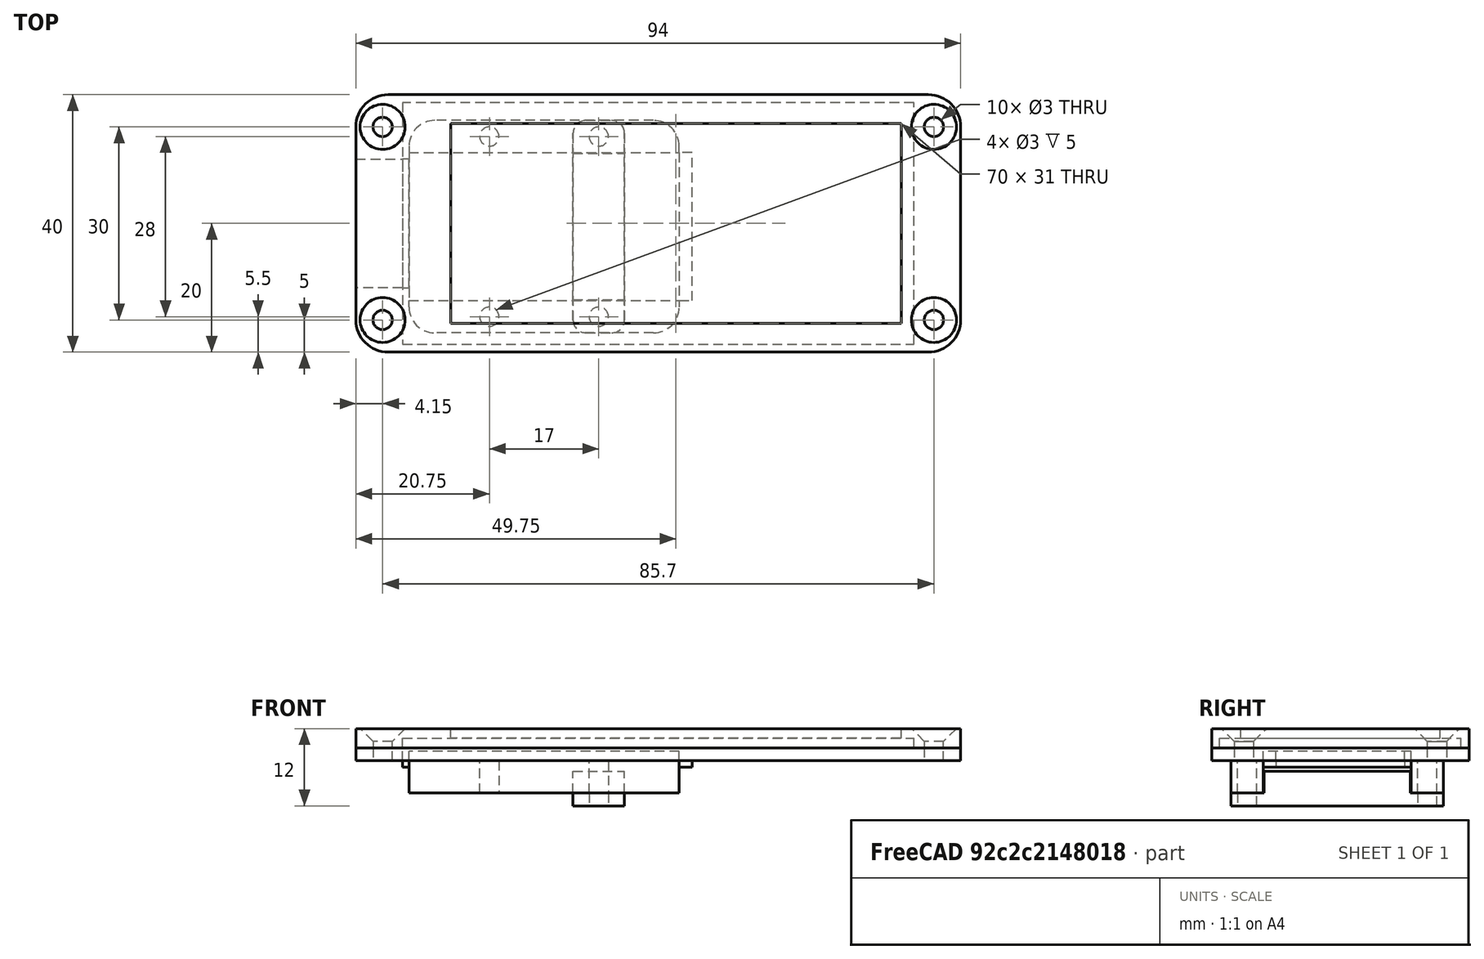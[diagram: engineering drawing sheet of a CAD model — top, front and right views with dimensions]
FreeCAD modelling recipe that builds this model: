
FCSTD DOCUMENT  (FreeCAD 0.19R)
Label: CrocSaintGerard
License: All rights reserved
LicenseURL: http://en.wikipedia.org/wiki/All_rights_reserved
objects: Sketcher::SketchObject×23, PartDesign::Pad×11, PartDesign::Body×8, PartDesign::Pocket×6, PartDesign::Fillet×6, PartDesign::Revolution×2, PartDesign::Chamfer×1, App::VRMLObject×1, Part::Helix×1, PartDesign::ShapeBinder×1, PartDesign::AdditivePipe×1, PartDesign::LinearPattern×1, App::DocumentObjectGroup×1, Mesh::Feature×1
note: 88 computed .brp shape members not serialized (recipe doc carries the construction recipe); baked Part::Feature solids carry a one-line shape summary decoded from their .brp

FEATURE [Sketcher::SketchObject] Sketch
  FullyConstrained = false
  MapMode = 5
  Support = -> [XY_Plane]
  sketch-geometry (17):
    g0: LineSegment StartX=-47 StartY=20 StartZ=0 EndX=47 EndY=20 EndZ=0
    g1: LineSegment StartX=47 StartY=20 StartZ=0 EndX=47 EndY=-20 EndZ=0
    g2: LineSegment StartX=47 StartY=-20 StartZ=0 EndX=-47 EndY=-20 EndZ=0
    g3: LineSegment StartX=-39.75 StartY=18.75 StartZ=0 EndX=39.75 EndY=18.75 EndZ=0
    g4: LineSegment StartX=39.75 StartY=18.75 StartZ=0 EndX=39.75 EndY=-18.75 EndZ=0
    g5: LineSegment StartX=39.75 StartY=-18.75 StartZ=0 EndX=-39.75 EndY=-18.75 EndZ=0
    g6: LineSegment StartX=-39.75 StartY=-18.75 StartZ=0 EndX=-39.75 EndY=18.75 EndZ=0
    g7: Circle CenterX=-42.85 CenterY=15 CenterZ=0 NormalX=0 NormalY=0 NormalZ=1 AngleXU=0 Radius=1.5
    g8: Circle CenterX=-42.85 CenterY=-15 CenterZ=0 NormalX=0 NormalY=0 NormalZ=1 AngleXU=0 Radius=1.5
    g9: Circle CenterX=42.85 CenterY=-15 CenterZ=0 NormalX=0 NormalY=0 NormalZ=1 AngleXU=0 Radius=1.5
    g10: Circle CenterX=42.85 CenterY=15 CenterZ=0 NormalX=0 NormalY=0 NormalZ=1 AngleXU=0 Radius=1.5
    g11: Circle CenterX=-42.85 CenterY=15 CenterZ=0 NormalX=0 NormalY=0 NormalZ=1 AngleXU=0 Radius=3
    g12: LineSegment StartX=-47 StartY=20 StartZ=0 EndX=-47 EndY=10 EndZ=0
    g13: LineSegment StartX=-47 StartY=10 StartZ=0 EndX=-39.75 EndY=10 EndZ=0
    g14: LineSegment StartX=-39.75 StartY=10 StartZ=0 EndX=-39.75 EndY=-10 EndZ=0
    g15: LineSegment StartX=-39.75 StartY=-10 StartZ=0 EndX=-47 EndY=-10 EndZ=0
    g16: LineSegment StartX=-47 StartY=-10 StartZ=0 EndX=-47 EndY=-20 EndZ=0
  constraints (44):
    c: Coincident(g0,g1)
    c: Coincident(g1,g2)
    c: Horizontal(g0)
    c: Horizontal(g2)
    c: Vertical(g1)
    c: Symmetric(g0,g1,g-1)
    c: DistanceY(g1,g1) = 40
    c: DistanceX(g0,g0) = 94
    c: Coincident(g3,g4)
    c: Coincident(g4,g5)
    c: Coincident(g5,g6)
    c: Coincident(g6,g3)
    c: Horizontal(g3)
    c: Horizontal(g5)
    c: Vertical(g4)
    c: Vertical(g6)
    c: Symmetric(g3,g4,g-1)
    c: DistanceY(g6,g6) = 37.5
    c: DistanceX(g3,g3) = 79.5
    c: Radius(g10) = 1.5
    c: Equal(g10,g9)
    c: Equal(g10,g8)
    c: Equal(g10,g7)
    c: Symmetric(g7,g8,g-1)
    c: Symmetric(g10,g9,g-1)
    c: Symmetric(g10,g7,g-2)
    c: Coincident(g11,g7)
    c: Radius(g11) = 3
    c: Coincident(g0,g12)
    c: Vertical(g12)
    c: Coincident(g12,g13)
    c: Horizontal(g13)
    c: Coincident(g13,g14)
    c: Vertical(g14)
    c: Coincident(g14,g15)
    c: Horizontal(g15)
    c: Coincident(g15,g16)
    c: Coincident(g16,g2)
    c: Vertical(g16)
    c: Symmetric(g15,g12,g-1)
    c: PointOnObject(g13,g6)
    c: DistanceY(g14,g14) = 20
    c: DistanceY(g-1,g7) = 15
    c: DistanceX(g-2,g7) = -42.85
FEATURE [PartDesign::Pad] Pad
  AllowMultiFace = false
  Direction = (1,1,1)
  Length = 2
  Length2 = 100
  Profile = -> Sketch
  Type = 0
FEATURE [Sketcher::SketchObject] Sketch001
  FullyConstrained = true
  MapMode = 5
  Support = -> [XY_Plane001]
  sketch-geometry (16):
    g0: LineSegment StartX=-47 StartY=20 StartZ=0 EndX=47 EndY=20 EndZ=0
    g1: LineSegment StartX=47 StartY=20 StartZ=0 EndX=47 EndY=-20 EndZ=0
    g2: LineSegment StartX=47 StartY=-20 StartZ=0 EndX=-47 EndY=-20 EndZ=0
    g3: LineSegment StartX=-47 StartY=-20 StartZ=0 EndX=-47 EndY=20 EndZ=0
    g4: Circle CenterX=-42.85 CenterY=15 CenterZ=0 NormalX=0 NormalY=0 NormalZ=1 AngleXU=0 Radius=1.5
    g5: Circle CenterX=-42.85 CenterY=-15 CenterZ=0 NormalX=0 NormalY=0 NormalZ=1 AngleXU=0 Radius=1.5
    g6: Circle CenterX=42.85 CenterY=15 CenterZ=0 NormalX=0 NormalY=0 NormalZ=1 AngleXU=0 Radius=1.5
    g7: Circle CenterX=42.85 CenterY=-15 CenterZ=0 NormalX=0 NormalY=0 NormalZ=1 AngleXU=0 Radius=1.5
    g8: LineSegment StartX=-32.25 StartY=15.5 StartZ=0 EndX=37.75 EndY=15.5 EndZ=0
    g9: LineSegment StartX=37.75 StartY=15.5 StartZ=0 EndX=37.75 EndY=-15.5 EndZ=0
    g10: LineSegment StartX=37.75 StartY=-15.5 StartZ=0 EndX=-32.25 EndY=-15.5 EndZ=0
    g11: LineSegment StartX=-32.25 StartY=-15.5 StartZ=0 EndX=-32.25 EndY=15.5 EndZ=0
    g12: LineSegment StartX=-39.75 StartY=18.75 StartZ=0 EndX=39.75 EndY=18.75 EndZ=0
    g13: LineSegment StartX=39.75 StartY=18.75 StartZ=0 EndX=39.75 EndY=-18.75 EndZ=0
    g14: LineSegment StartX=39.75 StartY=-18.75 StartZ=0 EndX=-39.75 EndY=-18.75 EndZ=0
    g15: LineSegment StartX=-39.75 StartY=-18.75 StartZ=0 EndX=-39.75 EndY=18.75 EndZ=0
  constraints (42):
    c: Coincident(g0,g1)
    c: Coincident(g1,g2)
    c: Coincident(g2,g3)
    c: Coincident(g3,g0)
    c: Horizontal(g0)
    c: Horizontal(g2)
    c: Vertical(g1)
    c: Vertical(g3)
    c: Symmetric(g1,g0,g-1)
    c: DistanceX(g0,g0) = 94
    c: DistanceY(g3,g3) = 40
    c: Radius(g4) = 1.5
    c: Equal(g4,g6)
    c: Equal(g4,g5)
    c: Equal(g4,g7)
    c: Symmetric(g5,g4,g-1)
    c: Symmetric(g6,g7,g-1)
    c: Symmetric(g4,g6,g-2)
    c: DistanceY(g-1,g4) = 15
    c: DistanceX(g-2,g4) = -42.85
    c: Coincident(g8,g9)
    c: Coincident(g9,g10)
    c: Coincident(g10,g11)
    c: Coincident(g11,g8)
    c: Horizontal(g8)
    c: Horizontal(g10)
    c: Vertical(g11)
    c: DistanceY(g9,g9) = 31
    c: DistanceX(g8,g8) = 70
    c: Symmetric(g8,g9,g-1)
    c: Coincident(g12,g13)
    c: Coincident(g13,g14)
    c: Coincident(g14,g15)
    c: Coincident(g15,g12)
    c: Horizontal(g12)
    c: Horizontal(g14)
    c: Vertical(g13)
    c: Vertical(g15)
    c: DistanceX(g12,g12) = 79.5
    c: Symmetric(g12,g13,g-1)
    c: DistanceY(g15,g15) = 37.5
    c: Distance(g8,g13) = 2
FEATURE [PartDesign::Pad] Pad001
  AllowMultiFace = false
  Direction = (1,1,1)
  Length = 3
  Length2 = 100
  Profile = -> Sketch001
  Type = 0
FEATURE [Sketcher::SketchObject] Sketch002
  FullyConstrained = true
  MapMode = 5
  Placement = pos=(0,0,0) rot=(1,0,0;3.14159rad)
  Support = -> [Pad001]
  sketch-geometry (4):
    g0: LineSegment StartX=-39.75 StartY=18.75 StartZ=0 EndX=39.75 EndY=18.75 EndZ=0
    g1: LineSegment StartX=39.75 StartY=18.75 StartZ=0 EndX=39.75 EndY=-18.75 EndZ=0
    g2: LineSegment StartX=39.75 StartY=-18.75 StartZ=0 EndX=-39.75 EndY=-18.75 EndZ=0
    g3: LineSegment StartX=-39.75 StartY=-18.75 StartZ=0 EndX=-39.75 EndY=18.75 EndZ=0
  constraints (11):
    c: Coincident(g0,g1)
    c: Coincident(g1,g2)
    c: Coincident(g2,g3)
    c: Coincident(g3,g0)
    c: Horizontal(g0)
    c: Horizontal(g2)
    c: Vertical(g1)
    c: Vertical(g3)
    c: DistanceY(g1,g1) = 37.5
    c: DistanceX(g0,g0) = 79.5
    c: Symmetric(g0,g2,g-1)
FEATURE [PartDesign::Pocket] Pocket
  AllowMultiFace = false
  BaseFeature = -> Pad001
  Length = 1.5
  Length2 = 100
  Profile = -> Sketch002
  Type = 0
FEATURE [PartDesign::Fillet] Fillet
  Base = -> Pocket [Edge5,Edge1,Edge8,Edge2]
  BaseFeature = -> Pocket
  Radius = 5
  SupportTransform = false
FEATURE [PartDesign::Fillet] Fillet001
  Base = -> Pad [Edge8,Edge5,Edge11,Edge1]
  BaseFeature = -> Pad
  Radius = 5
  SupportTransform = false
FEATURE [PartDesign::Chamfer] Chamfer
  Angle = 45
  Base = -> Fillet [Edge33,Edge34,Edge35,Edge36]
  BaseFeature = -> Fillet
  ChamferType = 0
  FlipDirection = false
  Size = 2
  Size2 = 1
  SupportTransform = false
FEATURE [PartDesign::Body] Body001  label="Devant"
  Group = -> [Sketch001,Pad001,Sketch002,Pocket,Fillet,Chamfer]
  Origin = -> Origin001
  Placement = pos=(77,-1,19) rot=(0,0,1;0rad)
  Tip = -> Chamfer
FEATURE [Sketcher::SketchObject] Sketch003
  ExternalGeometry = -> [Fillet001]
  FullyConstrained = false
  MapMode = 5
  Placement = pos=(0,0,0) rot=(1,0,0;3.14159rad)
  Support = -> [Fillet001]
  sketch-geometry (4):
    g0: LineSegment StartX=-38.75 StartY=12 StartZ=0 EndX=3.25 EndY=12 EndZ=0
    g1: LineSegment StartX=3.25 StartY=12 StartZ=0 EndX=3.25 EndY=-11 EndZ=0
    g2: LineSegment StartX=3.25 StartY=-11 StartZ=0 EndX=-38.75 EndY=-11 EndZ=0
    g3: LineSegment StartX=-38.75 StartY=-11 StartZ=0 EndX=-38.75 EndY=12 EndZ=0
  constraints (12):
    c: Coincident(g0,g1)
    c: Coincident(g1,g2)
    c: Coincident(g2,g3)
    c: Coincident(g3,g0)
    c: Horizontal(g0)
    c: Horizontal(g2)
    c: Vertical(g1)
    c: Vertical(g3)
    c: DistanceY(g1,g1) = 23
    c: DistanceX(g0,g0) = 42
    c: DistanceY(g-1,g0) = 12
    c: Distance(g0,g-3) = 1
FEATURE [PartDesign::Pocket] Pocket001
  AllowMultiFace = false
  BaseFeature = -> Fillet001
  Length = 1.5
  Length2 = 100
  Profile = -> Sketch003
  Type = 0
FEATURE [Sketcher::SketchObject] Sketch004
  ExternalGeometry = -> [Pocket001]
  FullyConstrained = false
  MapMode = 5
  Placement = pos=(0,0,0) rot=(1,0,0;3.14159rad)
  Support = -> [Pocket001]
  sketch-geometry (18):
    g0: LineSegment StartX=-38.75 StartY=12 StartZ=0 EndX=3.25 EndY=12 EndZ=0
    g1: LineSegment StartX=3.25 StartY=12 StartZ=0 EndX=3.25 EndY=17 EndZ=0
    g2: LineSegment StartX=3.25 StartY=17 StartZ=0 EndX=-38.75 EndY=17 EndZ=0
    g3: LineSegment StartX=-38.75 StartY=17 StartZ=0 EndX=-38.75 EndY=12 EndZ=0
    g4: LineSegment StartX=-38.75 StartY=-11 StartZ=0 EndX=3.25 EndY=-11 EndZ=0
    g5: LineSegment StartX=3.25 StartY=-11 StartZ=0 EndX=3.25 EndY=-16 EndZ=0
    g6: LineSegment StartX=3.25 StartY=-16 StartZ=0 EndX=-38.75 EndY=-16 EndZ=0
    g7: LineSegment StartX=-38.75 StartY=-16 StartZ=0 EndX=-38.75 EndY=-11 EndZ=0
    g8: Circle CenterX=-26.25 CenterY=14.5 CenterZ=0 NormalX=0 NormalY=0 NormalZ=1 AngleXU=0 Radius=1.5
    g9: Circle CenterX=-9.25 CenterY=14.5 CenterZ=0 NormalX=0 NormalY=0 NormalZ=1 AngleXU=0 Radius=1.5
    g10: Circle CenterX=-26.25 CenterY=-13.5 CenterZ=0 NormalX=0 NormalY=0 NormalZ=1 AngleXU=0 Radius=1.5
    g11: Circle CenterX=-9.25 CenterY=-13.5 CenterZ=0 NormalX=0 NormalY=0 NormalZ=1 AngleXU=0 Radius=1.5
    g12: LineSegment StartX=-38.75 StartY=14.5 StartZ=0 EndX=3.25 EndY=14.5 EndZ=0
    g13: LineSegment StartX=-38.75 StartY=14.5 StartZ=0 EndX=-38.75 EndY=17 EndZ=0
    g14: LineSegment StartX=-38.75 StartY=14.5 StartZ=0 EndX=-38.7607 EndY=12 EndZ=0
    g15: LineSegment StartX=-38.75 StartY=-13.5 StartZ=0 EndX=3.25 EndY=-13.5 EndZ=0
    g16: LineSegment StartX=-38.75 StartY=-11 StartZ=0 EndX=-38.75 EndY=-13.1302 EndZ=0
    g17: LineSegment StartX=-38.75 StartY=-16 StartZ=0 EndX=-38.75 EndY=-13.5 EndZ=0
  constraints (47):
    c: Coincident(g0,g1)
    c: Coincident(g1,g2)
    c: Coincident(g2,g3)
    c: Coincident(g3,g0)
    c: Horizontal(g2)
    c: Vertical(g1)
    c: Vertical(g3)
    c: Coincident(g0,g-3)
    c: Coincident(g4,g5)
    c: Coincident(g5,g6)
    c: Coincident(g6,g7)
    c: Coincident(g7,g4)
    c: Horizontal(g6)
    c: Vertical(g5)
    c: Vertical(g7)
    c: Coincident(g4,g-4)
    c: Coincident(g4,g-4)
    c: Coincident(g0,g-3)
    c: Equal(g1,g5)
    c: DistanceY(g1,g1) = 5
    c: Radius(g11) = 1.5
    c: Equal(g11,g10)
    c: Equal(g11,g8)
    c: Equal(g11,g9)
    c: PointOnObject(g12,g3)
    c: PointOnObject(g12,g1)
    c: Horizontal(g12)
    c: Coincident(g13,g12)
    c: Coincident(g13,g2)
    c: PointOnObject(g8,g12)
    c: PointOnObject(g9,g12)
    c: Distance(g14) = 2.5
    c: Coincident(g14,g12)
    c: Distance(g8,g3) = 12.5
    c: Distance(g9,g1) = 12.5
    c: PointOnObject(g15,g7)
    c: PointOnObject(g15,g5)
    c: Horizontal(g15)
    c: Coincident(g16,g4)
    c: PointOnObject(g10,g15)
    c: PointOnObject(g11,g15)
    c: Distance(g10,g7) = 12.5
    c: Distance(g11,g5) = 12.5
    c: Coincident(g17,g6)
    c: Distance(g17) = 2.5
    c: Coincident(g17,g15)
    c: Distance(g13) = 2.5
FEATURE [PartDesign::Pad] Pad002
  AllowMultiFace = false
  BaseFeature = -> Pocket001
  Direction = (1,1,1)
  Length = 5
  Length2 = 100
  Profile = -> Sketch004
  Type = 0
FEATURE [PartDesign::Fillet] Fillet002
  Base = -> Pad002 [Edge58,Edge66,Edge55,Edge68]
  BaseFeature = -> Pad002
  Radius = 4
  SupportTransform = false
FEATURE [Sketcher::SketchObject] Sketch005
  FullyConstrained = false
  MapMode = 5
  Placement = pos=(0,0,0) rot=(0.57735,0.57735,0.57735;2.0944rad)
  Support = -> [YZ_Plane002]
  sketch-geometry (8):
    g0: LineSegment StartX=-17 StartY=-5 StartZ=0 EndX=-11.875 EndY=-5 EndZ=0
    g1: LineSegment StartX=-11.875 StartY=-5 StartZ=0 EndX=-11.875 EndY=-1.6 EndZ=0
    g2: LineSegment StartX=-11.875 StartY=-1.6 StartZ=0 EndX=10.875 EndY=-1.6 EndZ=0
    g3: LineSegment StartX=10.875 StartY=-1.6 StartZ=0 EndX=10.875 EndY=-5 EndZ=0
    g4: LineSegment StartX=10.875 StartY=-5 StartZ=0 EndX=16 EndY=-5 EndZ=0
    g5: LineSegment StartX=16 StartY=-5 StartZ=0 EndX=16 EndY=-7 EndZ=0
    g6: LineSegment StartX=16 StartY=-7 StartZ=0 EndX=-17 EndY=-7 EndZ=0
    g7: LineSegment StartX=-17 StartY=-7 StartZ=0 EndX=-17 EndY=-5 EndZ=0
  constraints (24):
    c: Horizontal(g0)
    c: Coincident(g0,g1)
    c: Vertical(g1)
    c: Coincident(g1,g2)
    c: Horizontal(g2)
    c: Coincident(g2,g3)
    c: Vertical(g3)
    c: Coincident(g3,g4)
    c: Horizontal(g4)
    c: Coincident(g4,g5)
    c: Vertical(g5)
    c: Coincident(g5,g6)
    c: Horizontal(g6)
    c: Coincident(g6,g7)
    c: Coincident(g7,g0)
    c: Vertical(g7)
    c: DistanceY(g7,g7) = 2
    c: DistanceY(g1,g1) = 3.4
    c: DistanceX(g2,g2) = 22.75
    c: DistanceX(g0,g0) = 5.125
    c: Equal(g0,g4)
    c: Equal(g5,g7)
    c: DistanceY(g-1,g0) = -5
    c: DistanceX(g-2,g6) = -17
FEATURE [PartDesign::Pad] Pad003
  AllowMultiFace = false
  Direction = (1,1,1)
  Length = 8
  Length2 = 100
  Placement = pos=(0,0,0) rot=(0.57735,0.57735,0.57735;2.0944rad)
  Profile = -> Sketch005
  Type = 0
FEATURE [Sketcher::SketchObject] Sketch006
  ExternalGeometry = -> [Pad003]
  FullyConstrained = false
  MapMode = 5
  Placement = pos=(2e-15,-3.1e-15,-7) rot=(0.707107,0.707107,0;3.14159rad)
  Support = -> [Pad003]
  sketch-geometry (2):
    g0: Circle CenterX=-14.5 CenterY=4 CenterZ=0 NormalX=0 NormalY=0 NormalZ=1 AngleXU=0 Radius=1.5
    g1: Circle CenterX=13.5 CenterY=4 CenterZ=0 NormalX=0 NormalY=0 NormalZ=1 AngleXU=0 Radius=1.5
  constraints (6):
    c: Radius(g1) = 1.5
    c: Equal(g1,g0)
    c: DistanceY(g-1,g1) = 4
    c: DistanceY(g-1,g0) = 4
    c: Distance(g0,g-3) = 2.5
    c: Distance(g1,g-4) = 2.5
FEATURE [PartDesign::Pocket] Pocket002
  AllowMultiFace = false
  BaseFeature = -> Pad003
  Length = 5
  Length2 = 100
  Placement = pos=(0,0,0) rot=(0.57735,0.57735,0.57735;2.0944rad)
  Profile = -> Sketch006
  Type = 0
FEATURE [PartDesign::Fillet] Fillet003
  Base = -> Pocket002 [Edge8,Edge7,Edge19,Edge13]
  BaseFeature = -> Pocket002
  Placement = pos=(0,0,0) rot=(0.57735,0.57735,0.57735;2.0944rad)
  Radius = 2
  SupportTransform = false
FEATURE [PartDesign::Body] Body002  label="Attache"
  Group = -> [Sketch005,Pad003,Sketch006,Pocket002,Fillet003]
  Origin = -> Origin002
  Placement = pos=(63.75,-1,17) rot=(0,0,1;0rad)
  Tip = -> Fillet003
FEATURE [Sketcher::SketchObject] Sketch007
  ExternalGeometry = -> [Fillet002]
  FullyConstrained = false
  MapMode = 5
  Placement = pos=(0,0,0) rot=(1,0,0;3.14159rad)
  Support = -> [Fillet002]
  sketch-geometry (8):
    g0: LineSegment StartX=-39.75 StartY=10 StartZ=0 EndX=-38.75 EndY=10 EndZ=0
    g1: LineSegment StartX=-38.75 StartY=10 StartZ=0 EndX=-38.75 EndY=-10 EndZ=0
    g2: LineSegment StartX=-38.75 StartY=-10 StartZ=0 EndX=-39.75 EndY=-10 EndZ=0
    g3: LineSegment StartX=-39.75 StartY=-10 StartZ=0 EndX=-39.75 EndY=10 EndZ=0
    g4: LineSegment StartX=3.25 StartY=12 StartZ=0 EndX=5.25 EndY=12 EndZ=0
    g5: LineSegment StartX=5.25 StartY=12 StartZ=0 EndX=5.25 EndY=-11 EndZ=0
    g6: LineSegment StartX=5.25 StartY=-11 StartZ=0 EndX=3.25 EndY=-11 EndZ=0
    g7: LineSegment StartX=3.25 StartY=-11 StartZ=0 EndX=3.25 EndY=12 EndZ=0
  constraints (20):
    c: Coincident(g0,g1)
    c: Coincident(g1,g2)
    c: Coincident(g2,g3)
    c: Coincident(g3,g0)
    c: Horizontal(g0)
    c: Horizontal(g2)
    c: Vertical(g1)
    c: Coincident(g0,g-4)
    c: PointOnObject(g1,g-3)
    c: Coincident(g2,g-4)
    c: Coincident(g4,g5)
    c: Coincident(g5,g6)
    c: Coincident(g6,g7)
    c: Coincident(g7,g4)
    c: Horizontal(g4)
    c: Horizontal(g6)
    c: Vertical(g5)
    c: Coincident(g4,g-5)
    c: Coincident(g6,g-5)
    c: DistanceX(g6,g6) = 2
FEATURE [PartDesign::Pad] Pad004
  AllowMultiFace = false
  BaseFeature = -> Fillet002
  Direction = (1,1,1)
  Length = 1
  Length2 = 100
  Profile = -> Sketch007
  Type = 0
FEATURE [PartDesign::Body] Body  label="Plaque"
  Group = -> [Sketch,Pad,Fillet001,Sketch003,Pocket001,Sketch004,Pad002,Fillet002,Sketch007,Pad004]
  Origin = -> Origin
  Placement = pos=(77,-1,17) rot=(0,0,1;0rad)
  Tip = -> Pad004
FEATURE [App::VRMLObject] CroqueLivreSaintGerard2021_V1
  Placement = pos=(-73.3,92.8,-8.8) rot=(0,0,1;0rad)
  Resources = CroqueLivreSaintGerard2021_V1/CP_Radial_D12.5mm_P5.00mm.wrl | CroqueLivreSaintGerard2021_V1/ | CroqueLivreSaintGerard2021_V1/ | CroqueLivreSaintGerard2021_V1/ | CroqueLivreSaintGerard2021_V1/ | CroqueLivreSaintGerard2021_V1/ | CroqueLivreSaintGerard2021_V1/ | CroqueLivreSaintGerard2021_V1/ | CroqueLivreSaintGerard2021_V1/ | CroqueLivreSaintGerard2021_V1/ | CroqueLivreSaintGerard2021_V1/ | CroqueLivreSaintGerard2021_V1/
FEATURE [Sketcher::SketchObject] Sketch008
  FullyConstrained = false
  MapMode = 5
  Support = -> [XY_Plane003]
  sketch-geometry (11):
    g0: ArcOfCircle CenterX=-127.4 CenterY=0 CenterZ=0 NormalX=0 NormalY=0 NormalZ=1 AngleXU=0 Radius=42.5 StartAngle=1.5708 EndAngle=3.14159
    g1: ArcOfCircle CenterX=-127.4 CenterY=0 CenterZ=0 NormalX=0 NormalY=0 NormalZ=1 AngleXU=0 Radius=38.5 StartAngle=1.5708 EndAngle=3.14159
    g2: LineSegment StartX=-127.4 StartY=38.5 StartZ=0 EndX=-27.4 EndY=38.5 EndZ=0
    g3: ArcOfCircle CenterX=-24.2871 CenterY=39.1905 CenterZ=0 NormalX=0 NormalY=0 NormalZ=1 AngleXU=0 Radius=3.18854 StartAngle=3.35987 EndAngle=5.2334
    g4: LineSegment StartX=-22.7 StartY=36.425 StartZ=0 EndX=0 EndY=36.425 EndZ=0
    g5: LineSegment StartX=-127.4 StartY=42.5 StartZ=0 EndX=-27.4 EndY=42.5 EndZ=0
    g6: ArcOfCircle CenterX=-22.7 CenterY=43.802 CenterZ=0 NormalX=0 NormalY=0 NormalZ=1 AngleXU=0 Radius=4.87701 StartAngle=3.41184 EndAngle=4.71239
    g7: LineSegment StartX=-22.7 StartY=38.925 StartZ=0 EndX=-22.7 EndY=40.425 EndZ=0
    g8: LineSegment StartX=-22.7 StartY=40.425 StartZ=0 EndX=0 EndY=40.425 EndZ=0
    g9: LineSegment StartX=0 StartY=40.425 StartZ=0 EndX=0 EndY=36.425 EndZ=0
    g10: LineSegment StartX=-165.9 StartY=4.7e-15 StartZ=0 EndX=-169.9 EndY=5.2e-15 EndZ=0
  constraints (35):
    c: PointOnObject(g0,g-1)
    c: PointOnObject(g0,g-1)
    c: Coincident(g1,g0)
    c: PointOnObject(g1,g-1)
    c: Angle(g1) = 1.5708
    c: Angle(g0) = 1.5708
    c: Tangent(g1,g2) = 1.5708
    c: Coincident(g3,g2)
    c: Coincident(g4,g3)
    c: PointOnObject(g4,g-2)
    c: Horizontal(g4)
    c: Coincident(g5,g0)
    c: Horizontal(g5)
    c: Coincident(g6,g5)
    c: Coincident(g6,g7)
    c: Coincident(g7,g8)
    c: PointOnObject(g8,g-2)
    c: Horizontal(g8)
    c: Coincident(g8,g9)
    c: Coincident(g9,g4)
    c: Coincident(g10,g0)
    c: DistanceX(g10,g10) = 4
    c: Radius(g0) = 42.5
    c: Coincident(g1,g10)
    c: DistanceY(g9,g9) = 4
    c: Perpendicular(g6,g7)
    c: Vertical(g7)
    c: DistanceY(g-1,g4) = 36.425
    c: Equal(g4,g8)
    c: DistanceX(g8,g8) = 22.7
    c: DistanceX(g-2,g5) = -27.4
    c: Equal(g2,g5)
    c: PointOnObject(g3,g6)
    c: DistanceY(g7,g7) = 1.5
    c: DistanceX(g5,g5) = 100
FEATURE [PartDesign::Revolution] Revolution
  AllowMultiFace = false
  Angle = 360
  Axis = (1,0,0)
  Base = (0,0,0)
  Profile = -> Sketch008
  ReferenceAxis = -> Sketch008 [H_Axis]
FEATURE [PartDesign::Body] Body003  label="Enceinte de verre"
  Group = -> [Sketch008,Revolution]
  Origin = -> Origin003
  Placement = pos=(2e-16,9.1e-15,0) rot=(0,0,1;3.14159rad)
  Tip = -> Revolution
FEATURE [Sketcher::SketchObject] Sketch009
  FullyConstrained = false
  MapMode = 5
  Placement = pos=(0,0,0) rot=(0.57735,0.57735,0.57735;2.0944rad)
  Support = -> [YZ_Plane004]
  sketch-geometry (1):
    g0: Circle CenterX=0 CenterY=0 CenterZ=0 NormalX=0 NormalY=0 NormalZ=1 AngleXU=0 Radius=9
  constraints (2):
    c: Coincident(g0,g-1)
    c: Radius(g0) = 9
FEATURE [PartDesign::Pad] Pad005
  AllowMultiFace = false
  Direction = (1,1,1)
  Length = 65
  Length2 = 100
  Placement = pos=(0,0,0) rot=(0.57735,0.57735,0.57735;2.0944rad)
  Profile = -> Sketch009
  Type = 0
FEATURE [PartDesign::Body] Body004  label="Batterie"
  Group = -> [Sketch009,Pad005]
  Origin = -> Origin004
  Placement = pos=(48,25,9) rot=(0,0,1;0rad)
  Tip = -> Pad005
FEATURE [Sketcher::SketchObject] Sketch012
  FullyConstrained = true
  MapMode = 5
  Support = -> [XY_Plane006]
  sketch-geometry (16):
    g0: LineSegment StartX=-42.5 StartY=27.5 StartZ=0 EndX=-50.5 EndY=27.5 EndZ=0
    g1: LineSegment StartX=-50.5 StartY=27.5 StartZ=0 EndX=-50.5 EndY=-27.5 EndZ=0
    g2: LineSegment StartX=-50.5 StartY=-27.5 StartZ=0 EndX=-42.5 EndY=-27.5 EndZ=0
    g3: LineSegment StartX=-42.5 StartY=-27.5 StartZ=0 EndX=-42.5 EndY=-19 EndZ=0
    g4: LineSegment StartX=-42.5 StartY=-19 StartZ=0 EndX=-39.35 EndY=-19 EndZ=0
    g5: LineSegment StartX=-39.35 StartY=-19 StartZ=0 EndX=-39.35 EndY=-11 EndZ=0
    g6: LineSegment StartX=-39.35 StartY=-11 StartZ=0 EndX=-45.5 EndY=-11 EndZ=0
    g7: LineSegment StartX=-45.5 StartY=-11 StartZ=0 EndX=-45.5 EndY=11 EndZ=0
    g8: LineSegment StartX=-45.5 StartY=11 StartZ=0 EndX=-39.35 EndY=11 EndZ=0
    g9: LineSegment StartX=-39.35 StartY=11 StartZ=0 EndX=-39.35 EndY=19 EndZ=0
    g10: LineSegment StartX=-39.35 StartY=19 StartZ=0 EndX=-42.5 EndY=19 EndZ=0
    g11: LineSegment StartX=-42.5 StartY=19 StartZ=0 EndX=-42.5 EndY=27.5 EndZ=0
    g12: Circle CenterX=-46.5 CenterY=23.05 CenterZ=0 NormalX=0 NormalY=0 NormalZ=1 AngleXU=0 Radius=1.5
    g13: Circle CenterX=-46.5 CenterY=-23.05 CenterZ=0 NormalX=0 NormalY=0 NormalZ=1 AngleXU=0 Radius=1.5
    g14: Circle CenterX=-42.85 CenterY=15 CenterZ=0 NormalX=0 NormalY=0 NormalZ=1 AngleXU=0 Radius=1.5
    g15: Circle CenterX=-42.85 CenterY=-15 CenterZ=0 NormalX=0 NormalY=0 NormalZ=1 AngleXU=0 Radius=1.5
  constraints (43):
    c: Horizontal(g0)
    c: Coincident(g0,g1)
    c: Vertical(g1)
    c: Coincident(g1,g2)
    c: Horizontal(g2)
    c: Coincident(g2,g3)
    c: Vertical(g3)
    c: Coincident(g3,g4)
    c: Coincident(g4,g5)
    c: Vertical(g5)
    c: Coincident(g5,g6)
    c: Horizontal(g6)
    c: Coincident(g6,g7)
    c: Coincident(g7,g8)
    c: Horizontal(g8)
    c: Coincident(g8,g9)
    c: Vertical(g9)
    c: Coincident(g9,g10)
    c: Coincident(g10,g11)
    c: Coincident(g11,g0)
    c: Vertical(g11)
    c: Symmetric(g2,g0,g-1)
    c: Horizontal(g10)
    c: Symmetric(g9,g4,g-1)
    c: Symmetric(g6,g7,g-1)
    c: Horizontal(g4)
    c: DistanceX(g-2,g0) = -50.5
    c: DistanceX(g0,g0) = 8
    c: DistanceY(g9,g9) = 8
    c: Distance(g7,g1) = 5
    c: Radius(g13) = 1.5
    c: Equal(g13,g12)
    c: Distance(g12,g13) = 46.1
    c: Symmetric(g12,g13,g-1)
    c: Distance(g13,g1) = 4
    c: Symmetric(g15,g14,g-1)
    c: Radius(g14) = 1.5
    c: Equal(g14,g15)
    c: Distance(g14,g9) = 3.5
    c: DistanceX(g-2,g14) = -42.85
    c: DistanceY(g1,g1) = 55
    c: Distance(g14,g10) = 4
    c: DistanceY(g-1,g14) = 15
FEATURE [PartDesign::Pad] Pad006
  Direction = (1,1,1)
  Length = 10
  Length2 = 100
  Profile = -> Sketch012
  Type = 0
FEATURE [Sketcher::SketchObject] Sketch013
  ExternalGeometry = -> [Pad006]
  FullyConstrained = true
  MapMode = 5
  Placement = pos=(-50.5,0,0) rot=(0.57735,-0.57735,-0.57735;2.0944rad)
  Support = -> [Pad006]
  sketch-geometry (4):
    g0: LineSegment StartX=-10 StartY=10 StartZ=0 EndX=10 EndY=10 EndZ=0
    g1: LineSegment StartX=10 StartY=10 StartZ=0 EndX=10 EndY=5 EndZ=0
    g2: LineSegment StartX=10 StartY=5 StartZ=0 EndX=-10 EndY=5 EndZ=0
    g3: LineSegment StartX=-10 StartY=5 StartZ=0 EndX=-10 EndY=10 EndZ=0
  constraints (11):
    c: Coincident(g0,g1)
    c: Coincident(g1,g2)
    c: Coincident(g2,g3)
    c: Coincident(g3,g0)
    c: Horizontal(g2)
    c: Vertical(g1)
    c: Vertical(g3)
    c: PointOnObject(g0,g-3)
    c: DistanceY(g3,g3) = 5
    c: Symmetric(g0,g0,g-2)
    c: DistanceX(g0,g0) = 20
FEATURE [PartDesign::Pocket] Pocket003
  BaseFeature = -> Pad006
  Length = 6
  Length2 = 100
  Profile = -> Sketch013
  Type = 0
FEATURE [Sketcher::SketchObject] Sketch014
  ExternalGeometry = -> [Pocket003]
  FullyConstrained = true
  MapMode = 5
  Placement = pos=(0,0,0) rot=(1,0,0;3.14159rad)
  Support = -> [Pocket003]
  sketch-geometry (10):
    g0: Circle CenterX=-46.5 CenterY=-23.05 CenterZ=0 NormalX=0 NormalY=0 NormalZ=1 AngleXU=0 Radius=1.5
    g1: Circle CenterX=-46.5 CenterY=23.05 CenterZ=0 NormalX=0 NormalY=0 NormalZ=1 AngleXU=0 Radius=1.5
    g2: LineSegment StartX=-50.5 StartY=27.5 StartZ=0 EndX=-42.5 EndY=27.5 EndZ=0
    g3: LineSegment StartX=-42.5 StartY=27.5 StartZ=0 EndX=-42.5 EndY=19 EndZ=0
    g4: LineSegment StartX=-42.5 StartY=19 StartZ=0 EndX=-50.5 EndY=19 EndZ=0
    g5: LineSegment StartX=-50.5 StartY=19 StartZ=0 EndX=-50.5 EndY=27.5 EndZ=0
    g6: LineSegment StartX=-42.5 StartY=-19 StartZ=0 EndX=-50.5 EndY=-19 EndZ=0
    g7: LineSegment StartX=-50.5 StartY=-19 StartZ=0 EndX=-50.5 EndY=-27.5 EndZ=0
    g8: LineSegment StartX=-50.5 StartY=-27.5 StartZ=0 EndX=-42.5 EndY=-27.5 EndZ=0
    g9: LineSegment StartX=-42.5 StartY=-27.5 StartZ=0 EndX=-42.5 EndY=-19 EndZ=0
  constraints (24):
    c: Coincident(g0,g-4)
    c: Coincident(g1,g-3)
    c: Radius(g1) = 1.5
    c: Equal(g1,g0)
    c: Coincident(g2,g3)
    c: Coincident(g3,g4)
    c: Coincident(g4,g5)
    c: Coincident(g5,g2)
    c: Horizontal(g2)
    c: Horizontal(g4)
    c: Vertical(g3)
    c: Vertical(g5)
    c: Coincident(g2,g-5)
    c: Coincident(g3,g-6)
    c: Coincident(g6,g7)
    c: Coincident(g7,g8)
    c: Coincident(g8,g9)
    c: Coincident(g9,g6)
    c: Horizontal(g6)
    c: Horizontal(g8)
    c: Vertical(g7)
    c: Vertical(g9)
    c: Coincident(g6,g-7)
    c: Coincident(g7,g-8)
FEATURE [PartDesign::Pad] Pad007
  BaseFeature = -> Pocket003
  Direction = (1,1,1)
  Length = 15
  Length2 = 100
  Profile = -> Sketch014
  Type = 0
FEATURE [PartDesign::Fillet] Fillet004
  Base = -> Pad007 [Edge43,Edge44,Edge11,Edge76,Edge18,Edge31,Edge17]
  BaseFeature = -> Pad007
  Radius = 3
  SupportTransform = false
FEATURE [Sketcher::SketchObject] Sketch018
  FullyConstrained = true
  MapMode = 5
  Support = -> [XY_Plane008]
  sketch-geometry (2):
    g0: Circle CenterX=0 CenterY=0 CenterZ=0 NormalX=0 NormalY=0 NormalZ=1 AngleXU=0 Radius=42.25
    g1: Circle CenterX=0 CenterY=0 CenterZ=0 NormalX=0 NormalY=0 NormalZ=1 AngleXU=0 Radius=45
  constraints (4):
    c: Coincident(g0,g-1)
    c: Coincident(g1,g0)
    c: Radius(g0) = 42.25
    c: Radius(g1) = 45
FEATURE [Part::Helix] Helix
  Angle = 0
  AttacherType = Attacher::AttachEngine3D
  Height = 6.22
  LocalCoord = 0
  Pitch = 6.23
  Radius = 40.5
  Style = 1
FEATURE [Sketcher::SketchObject] Sketch019
  FullyConstrained = true
  MapMode = 5
  Support = -> [XY_Plane008]
FEATURE [PartDesign::Pad] Pad010
  Direction = (1,1,1)
  Length = 20
  Length2 = 100
  Profile = -> Sketch018
  Type = 0
FEATURE [Sketcher::SketchObject] Sketch020  label="Profile"
  FullyConstrained = true
  MapMode = 5
  Placement = pos=(0,0,0) rot=(1,0,0;1.5708rad)
  Support = -> [XZ_Plane008]
  sketch-geometry (7):
    g0: LineSegment StartX=42.25 StartY=4.40427 StartZ=0 EndX=40.9557 EndY=3.11 EndZ=0
    g1: LineSegment StartX=40.9557 StartY=3.11 StartZ=0 EndX=40.9557 EndY=1.29427 EndZ=0
    g2: LineSegment StartX=40.9557 StartY=1.29427 StartZ=0 EndX=42.25 EndY=0 EndZ=0
    g3: LineSegment StartX=42.25 StartY=4.40427 StartZ=0 EndX=42.25 EndY=6.22 EndZ=0
    g4: LineSegment StartX=42.25 StartY=6.22 StartZ=0 EndX=43.25 EndY=6.22 EndZ=0
    g5: LineSegment StartX=43.25 StartY=6.22 StartZ=0 EndX=43.25 EndY=0 EndZ=0
    g6: LineSegment StartX=43.25 StartY=0 StartZ=0 EndX=42.25 EndY=0 EndZ=0
  constraints (21):
    c: Coincident(g0,g1)
    c: Vertical(g1)
    c: Coincident(g1,g2)
    c: DistanceX(g-2,g2) = 42.25
    c: PointOnObject(g2,g-1)
    c: Coincident(g0,g3)
    c: Vertical(g3)
    c: Coincident(g3,g4)
    c: Horizontal(g4)
    c: Coincident(g4,g5)
    c: PointOnObject(g5,g-1)
    c: Vertical(g5)
    c: Coincident(g5,g6)
    c: Coincident(g6,g2)
    c: DistanceX(g4,g4) = 1
    c: Equal(g3,g1)
    c: Equal(g2,g0)
    c: Angle(g2,g-1) = 0.785398
    c: Equal(g1,g3)
    c: DistanceY(g5,g5) = 6.22
    c: DistanceX(g-2,g0) = 42.25
FEATURE [PartDesign::ShapeBinder] ShapeBinder
  Support = -> [Helix]
  TraceSupport = false
FEATURE [PartDesign::AdditivePipe] AdditivePipe001
  AuxilleryCurvelinear = true
  AuxillerySpineTangent = false
  BaseFeature = -> Pad010
  Binormal = (0,0,0)
  Mode = 2
  Profile = -> Sketch020
  Spine = -> ShapeBinder
  SpineTangent = false
  Transformation = 0
  Transition = 0
FEATURE [PartDesign::LinearPattern] LinearPattern
  BaseFeature = -> AdditivePipe001
  Direction = -> Z_Axis008
  Length = 12.46
  Occurrences = 3
  Originals = -> [AdditivePipe001]
FEATURE [Sketcher::SketchObject] Sketch021
  FullyConstrained = true
  MapMode = 5
  Placement = pos=(0,0,0) rot=(1,0,0;1.5708rad)
  Support = -> [XZ_Plane008]
  sketch-geometry (4):
    g0: LineSegment StartX=-90 StartY=29.5 StartZ=0 EndX=90 EndY=29.5 EndZ=0
    g1: LineSegment StartX=90 StartY=29.5 StartZ=0 EndX=90 EndY=19.5 EndZ=0
    g2: LineSegment StartX=90 StartY=19.5 StartZ=0 EndX=-90 EndY=19.5 EndZ=0
    g3: LineSegment StartX=-90 StartY=19.5 StartZ=0 EndX=-90 EndY=29.5 EndZ=0
  constraints (11):
    c: Coincident(g0,g1)
    c: Coincident(g1,g2)
    c: Coincident(g2,g3)
    c: Coincident(g3,g0)
    c: Horizontal(g2)
    c: Vertical(g1)
    c: Vertical(g3)
    c: DistanceY(g-1,g1) = 19.5
    c: Symmetric(g0,g0,g-2)
    c: DistanceY(g1,g1) = 10
    c: DistanceX(g0,g0) = 180
FEATURE [PartDesign::Pocket] Pocket005
  BaseFeature = -> LinearPattern
  Length = 200
  Length2 = 100
  Midplane = true
  Profile = -> Sketch021
  Type = 0
FEATURE [Sketcher::SketchObject] Sketch022
  FullyConstrained = true
  MapMode = 5
  Placement = pos=(0,0,0) rot=(1,0,0;1.5708rad)
  Support = -> [XZ_Plane006]
FEATURE [PartDesign::Body] Body006  label="Support_ecran_PCB"
  Group = -> [Sketch012,Pad006,Sketch013,Pocket003,Sketch014,Pad007,Fillet004,Sketch022]
  Origin = -> Origin006
  Placement = pos=(77,-1,7) rot=(0,0,1;0rad)
  Tip = -> Fillet004
FEATURE [Sketcher::SketchObject] Sketch023
  FullyConstrained = true
  MapMode = 5
  Placement = pos=(0,0,0) rot=(0.57735,0.57735,0.57735;2.0944rad)
  Support = -> [YZ_Plane008]
  sketch-geometry (6):
    g0: ArcOfCircle CenterX=0 CenterY=0 CenterZ=0 NormalX=0 NormalY=0 NormalZ=1 AngleXU=0 Radius=45 StartAngle=3.14159 EndAngle=4.71239
    g1: ArcOfCircle CenterX=0 CenterY=0 CenterZ=0 NormalX=0 NormalY=0 NormalZ=1 AngleXU=0 Radius=41 StartAngle=3.23931 EndAngle=4.71239
    g2: LineSegment StartX=0 StartY=-41 StartZ=0 EndX=-8.3e-15 EndY=-45 EndZ=0
    g3: LineSegment StartX=-45 StartY=0 StartZ=0 EndX=-35 EndY=0 EndZ=0
    g4: LineSegment StartX=-40.8044 StartY=-4 StartZ=0 EndX=-35 EndY=-4 EndZ=0
    g5: LineSegment StartX=-35 StartY=-4 StartZ=0 EndX=-35 EndY=0 EndZ=0
  constraints (18):
    c: Coincident(g0,g-1)
    c: PointOnObject(g0,g-2)
    c: PointOnObject(g0,g-1)
    c: Radius(g0) = 45
    c: Coincident(g1,g0)
    c: PointOnObject(g1,g-2)
    c: Coincident(g2,g1)
    c: Coincident(g2,g0)
    c: Coincident(g1,g4)
    c: Coincident(g4,g5)
    c: Coincident(g5,g3)
    c: Horizontal(g3)
    c: Vertical(g5)
    c: DistanceX(g3,g3) = 10
    c: Horizontal(g4)
    c: Radius(g1) = 41
    c: DistanceY(g5,g5) = 4
    c: Coincident(g3,g0)
FEATURE [PartDesign::Revolution] Revolution001
  Angle = 360
  Axis = (-2e-16,3e-16,1)
  Base = (0,0,0)
  BaseFeature = -> Pocket005
  Profile = -> Sketch023
  ReferenceAxis = -> Sketch023 [V_Axis]
FEATURE [PartDesign::Body] Body008  label="Vis base"
  Group = -> [Sketch019,Sketch018,Pad010,Sketch020,ShapeBinder,AdditivePipe001,LinearPattern,Sketch021,Pocket005,Sketch023,Revolution001]
  Origin = -> Origin008
  Placement = pos=(0,0,0) rot=(0,-1,0;4.71239rad)
  Tip = -> Revolution001
FEATURE [Sketcher::SketchObject] Sketch024
  FullyConstrained = true
  MapMode = 5
  Support = -> [XY_Plane009]
  sketch-geometry (16):
    g0: LineSegment StartX=-42.5 StartY=27.5 StartZ=0 EndX=-50.5 EndY=27.5 EndZ=0
    g1: LineSegment StartX=-50.5 StartY=27.5 StartZ=0 EndX=-50.5 EndY=-27.5 EndZ=0
    g2: LineSegment StartX=-50.5 StartY=-27.5 StartZ=0 EndX=-42.5 EndY=-27.5 EndZ=0
    g3: LineSegment StartX=-42.5 StartY=-27.5 StartZ=0 EndX=-42.5 EndY=-19 EndZ=0
    g4: LineSegment StartX=-42.5 StartY=-19 StartZ=0 EndX=-39.35 EndY=-19 EndZ=0
    g5: LineSegment StartX=-39.35 StartY=-19 StartZ=0 EndX=-39.35 EndY=-11 EndZ=0
    g6: LineSegment StartX=-39.35 StartY=-11 StartZ=0 EndX=-45.5 EndY=-11 EndZ=0
    g7: LineSegment StartX=-45.5 StartY=-11 StartZ=0 EndX=-45.5 EndY=11 EndZ=0
    g8: LineSegment StartX=-45.5 StartY=11 StartZ=0 EndX=-39.35 EndY=11 EndZ=0
    g9: LineSegment StartX=-39.35 StartY=11 StartZ=0 EndX=-39.35 EndY=19 EndZ=0
    g10: LineSegment StartX=-39.35 StartY=19 StartZ=0 EndX=-42.5 EndY=19 EndZ=0
    g11: LineSegment StartX=-42.5 StartY=19 StartZ=0 EndX=-42.5 EndY=27.5 EndZ=0
    g12: Circle CenterX=-46.5 CenterY=23.05 CenterZ=0 NormalX=0 NormalY=0 NormalZ=1 AngleXU=0 Radius=1.5
    g13: Circle CenterX=-46.5 CenterY=-23.05 CenterZ=0 NormalX=0 NormalY=0 NormalZ=1 AngleXU=0 Radius=1.5
    g14: Circle CenterX=-42.85 CenterY=15 CenterZ=0 NormalX=0 NormalY=0 NormalZ=1 AngleXU=0 Radius=1.5
    g15: Circle CenterX=-42.85 CenterY=-15 CenterZ=0 NormalX=0 NormalY=0 NormalZ=1 AngleXU=0 Radius=1.5
  constraints (43):
    c: Horizontal(g0)
    c: Coincident(g0,g1)
    c: Vertical(g1)
    c: Coincident(g1,g2)
    c: Horizontal(g2)
    c: Coincident(g2,g3)
    c: Vertical(g3)
    c: Coincident(g3,g4)
    c: Coincident(g4,g5)
    c: Vertical(g5)
    c: Coincident(g5,g6)
    c: Horizontal(g6)
    c: Coincident(g6,g7)
    c: Coincident(g7,g8)
    c: Horizontal(g8)
    c: Coincident(g8,g9)
    c: Vertical(g9)
    c: Coincident(g9,g10)
    c: Coincident(g10,g11)
    c: Coincident(g11,g0)
    c: Vertical(g11)
    c: Symmetric(g2,g0,g-1)
    c: Horizontal(g10)
    c: Symmetric(g9,g4,g-1)
    c: Symmetric(g6,g7,g-1)
    c: Horizontal(g4)
    c: DistanceX(g-2,g0) = -50.5
    c: DistanceX(g0,g0) = 8
    c: DistanceY(g9,g9) = 8
    c: Distance(g7,g1) = 5
    c: Radius(g13) = 1.5
    c: Equal(g13,g12)
    c: Distance(g12,g13) = 46.1
    c: Symmetric(g12,g13,g-1)
    c: Distance(g13,g1) = 4
    c: Symmetric(g15,g14,g-1)
    c: Radius(g14) = 1.5
    c: Equal(g14,g15)
    c: Distance(g14,g9) = 3.5
    c: DistanceX(g-2,g14) = -42.85
    c: DistanceY(g1,g1) = 55
    c: Distance(g14,g10) = 4
    c: DistanceY(g-1,g14) = 15
FEATURE [PartDesign::Pad] Pad012
  Direction = (1,1,1)
  Length = 10
  Length2 = 100
  Profile = -> Sketch024
  Type = 0
FEATURE [Sketcher::SketchObject] Sketch025
  ExternalGeometry = -> [Pad012]
  FullyConstrained = true
  MapMode = 5
  Placement = pos=(-50.5,0,0) rot=(0.57735,-0.57735,-0.57735;2.0944rad)
  Support = -> [Pad012]
  sketch-geometry (4):
    g0: LineSegment StartX=-10 StartY=10 StartZ=0 EndX=10 EndY=10 EndZ=0
    g1: LineSegment StartX=10 StartY=10 StartZ=0 EndX=10 EndY=5 EndZ=0
    g2: LineSegment StartX=10 StartY=5 StartZ=0 EndX=-10 EndY=5 EndZ=0
    g3: LineSegment StartX=-10 StartY=5 StartZ=0 EndX=-10 EndY=10 EndZ=0
  constraints (11):
    c: Coincident(g0,g1)
    c: Coincident(g1,g2)
    c: Coincident(g2,g3)
    c: Coincident(g3,g0)
    c: Horizontal(g2)
    c: Vertical(g1)
    c: Vertical(g3)
    c: PointOnObject(g0,g-3)
    c: DistanceY(g3,g3) = 5
    c: Symmetric(g0,g0,g-2)
    c: DistanceX(g0,g0) = 20
FEATURE [PartDesign::Pocket] Pocket006
  BaseFeature = -> Pad012
  Length = 6
  Length2 = 100
  Profile = -> Sketch025
  Type = 0
FEATURE [Sketcher::SketchObject] Sketch026
  ExternalGeometry = -> [Pocket006]
  FullyConstrained = true
  MapMode = 5
  Placement = pos=(0,0,0) rot=(1,0,0;3.14159rad)
  Support = -> [Pocket006]
  sketch-geometry (10):
    g0: Circle CenterX=-46.5 CenterY=-23.05 CenterZ=0 NormalX=0 NormalY=0 NormalZ=1 AngleXU=0 Radius=1.5
    g1: Circle CenterX=-46.5 CenterY=23.05 CenterZ=0 NormalX=0 NormalY=0 NormalZ=1 AngleXU=0 Radius=1.5
    g2: LineSegment StartX=-50.5 StartY=27.5 StartZ=0 EndX=-42.5 EndY=27.5 EndZ=0
    g3: LineSegment StartX=-42.5 StartY=27.5 StartZ=0 EndX=-42.5 EndY=19 EndZ=0
    g4: LineSegment StartX=-42.5 StartY=19 StartZ=0 EndX=-50.5 EndY=19 EndZ=0
    g5: LineSegment StartX=-50.5 StartY=19 StartZ=0 EndX=-50.5 EndY=27.5 EndZ=0
    g6: LineSegment StartX=-42.5 StartY=-19 StartZ=0 EndX=-50.5 EndY=-19 EndZ=0
    g7: LineSegment StartX=-50.5 StartY=-19 StartZ=0 EndX=-50.5 EndY=-27.5 EndZ=0
    g8: LineSegment StartX=-50.5 StartY=-27.5 StartZ=0 EndX=-42.5 EndY=-27.5 EndZ=0
    g9: LineSegment StartX=-42.5 StartY=-27.5 StartZ=0 EndX=-42.5 EndY=-19 EndZ=0
  constraints (24):
    c: Coincident(g0,g-4)
    c: Coincident(g1,g-3)
    c: Radius(g1) = 1.5
    c: Equal(g1,g0)
    c: Coincident(g2,g3)
    c: Coincident(g3,g4)
    c: Coincident(g4,g5)
    c: Coincident(g5,g2)
    c: Horizontal(g2)
    c: Horizontal(g4)
    c: Vertical(g3)
    c: Vertical(g5)
    c: Coincident(g2,g-5)
    c: Coincident(g3,g-6)
    c: Coincident(g6,g7)
    c: Coincident(g7,g8)
    c: Coincident(g8,g9)
    c: Coincident(g9,g6)
    c: Horizontal(g6)
    c: Horizontal(g8)
    c: Vertical(g7)
    c: Vertical(g9)
    c: Coincident(g6,g-7)
    c: Coincident(g7,g-8)
FEATURE [PartDesign::Pad] Pad011
  BaseFeature = -> Pocket006
  Direction = (1,1,1)
  Length = 15
  Length2 = 100
  Profile = -> Sketch026
  Type = 0
FEATURE [PartDesign::Fillet] Fillet005
  Base = -> Pad011 [Edge43,Edge44,Edge11,Edge76,Edge18,Edge31,Edge17]
  BaseFeature = -> Pad011
  Radius = 3
  SupportTransform = false
FEATURE [Sketcher::SketchObject] Sketch027
  FullyConstrained = true
  MapMode = 5
  Placement = pos=(0,0,0) rot=(1,0,0;1.5708rad)
  Support = -> [XZ_Plane009]
FEATURE [PartDesign::Body] Body009  label="Support_ecran_PCB001"
  Group = -> [Sketch024,Pad012,Sketch025,Pocket006,Sketch026,Pad011,Fillet005,Sketch027]
  Origin = -> Origin009
  Placement = pos=(77,-1,7) rot=(0,0,1;3.14159rad)
  Tip = -> Fillet005
FEATURE [App::DocumentObjectGroup] Group
  Group = -> [Body002,Body001,Body006,Body009,CroqueLivreSaintGerard2021_V1]
FEATURE [Mesh::Feature] Mesh  label="Support_ecran_PCB (Meshed)"
